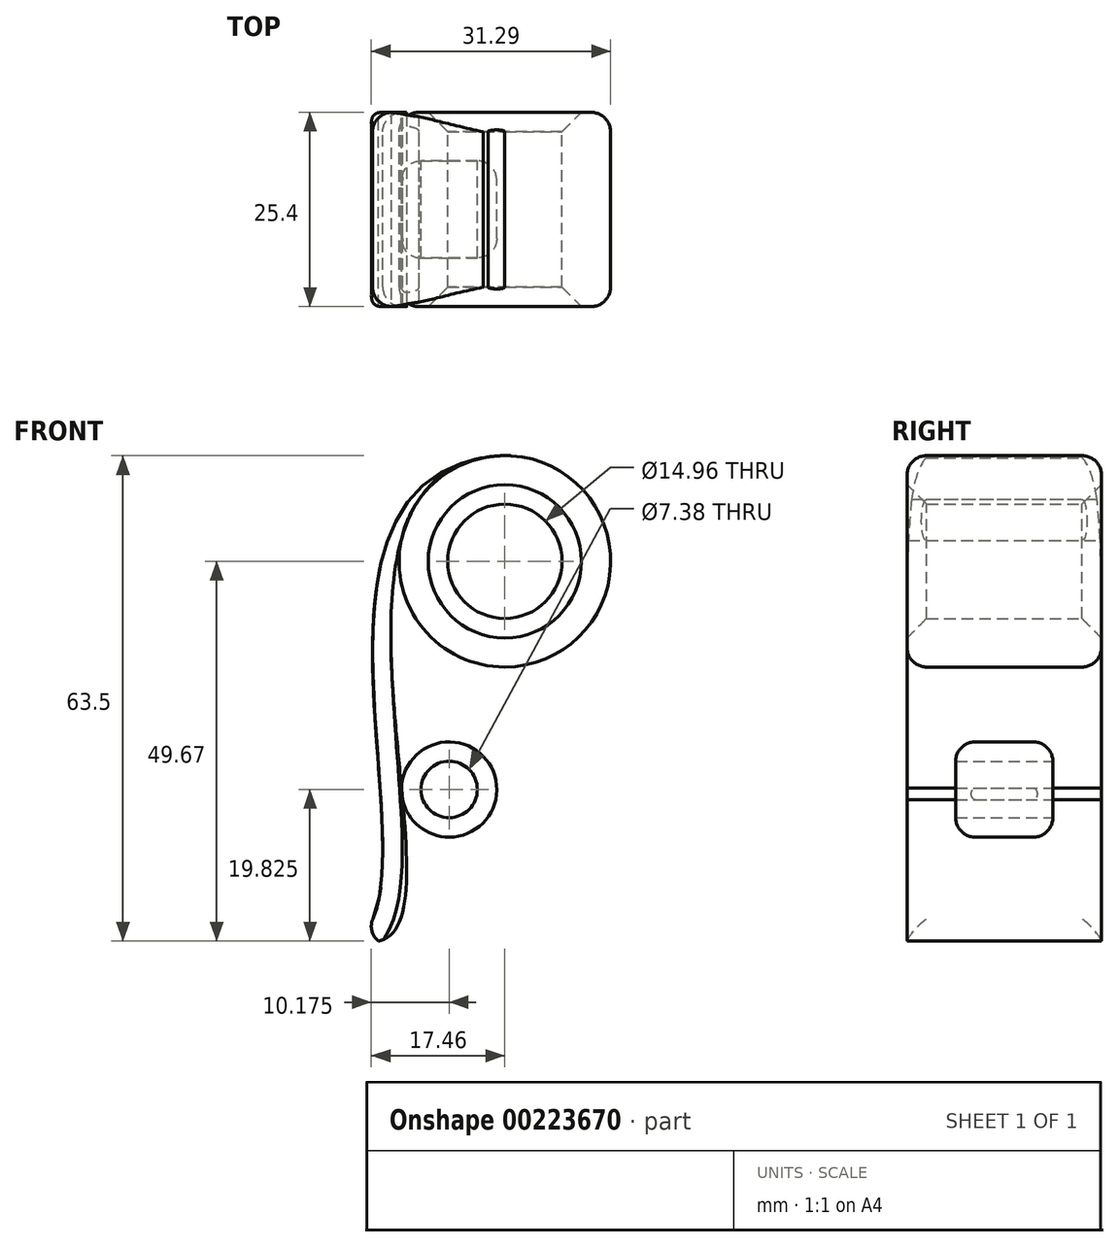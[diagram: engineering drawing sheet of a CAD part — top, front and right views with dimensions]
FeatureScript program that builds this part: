
annotation { "Feature Type Name" : "Feature", "Feature Type Description" : "" }
export const myFeature = defineFeature(function(context is Context, id is Id, definition is map)
    precondition{}
    {
        {
            var Q0;
            Q0=qCreatedBy(makeId("Front.planeOp"),FACE);
            var sketch = newSketch(context, id + "F0", { "sketchPlane" : qUnion([Q0])});
            skCircle(sketch, "E0", {"center": v(0, 0) * mm, "radius": 13.83 * mm});
            skCircle(sketch, "E1", {"center": v(0, 0) * mm, "radius": 7.48 * mm});
            skFitSpline(sketch, "E2", {"points": [v(0, 13.83) * mm, v(-16.56, -49.67) * mm], "startDerivative": vector(-87.8, -2.03) * mm, "endDerivative": vector(-37.2, -6.56) * mm});
            skCircle(sketch, "E3", {"center": v(-7.29, -29.84) * mm, "radius": 6.23 * mm});
            skCircle(sketch, "E4", {"center": v(-7.29, -29.84) * mm, "radius": 3.69 * mm});
            skFitSpline(sketch, "E5", {"points": [v(-2.73, 13.57) * mm, v(-20.14, -49.93) * mm], "startDerivative": vector(-83.92, -14.8) * mm, "endDerivative": vector(-38.31, -17.67) * mm});
            skLineSegment(sketch, "E6", {"start": v(-16.56, -49.67) * mm, "end": v(-20.14, -49.93) * mm});
            skSolve(sketch);
        }
        {
            var Q0;
            {var subQ0=sQuery(id+"F0.wireOp",EDGE,"E6");Q0=makeQuery(id+"F0.imprint","IMPRINT",FACE,{"disambiguationData":[TD([[makeQuery(id+"F0.imprint","IMPRINT",EDGE,{"derivedFrom":subQ0}),-1.0]])]});}
            extrude(context, id + "F1", {"entities" : qUnion([Q0]), "endBound" : BoundingType.SYMMETRIC, "depth" : 25.4 * mm});
        }
        {
            var Q0;
            Q0=makeQuery(id+"F0.imprint","IMPRINT",FACE,{"disambiguationData":[TD([[makeQuery(id+"F0.imprint","IMPRINT",EDGE,{"derivedFrom":sQuery(id+"F0.wireOp",EDGE,"E1")}),-1.0]])]});
            extrude(context, id + "F2", {"entities" : qUnion([Q0]), "endBound" : BoundingType.SYMMETRIC, "depth" : 25.4 * mm});
        }
        {
            var Q0;
            Q0=makeQuery(id+"F0.imprint","IMPRINT",FACE,{"disambiguationData":[TD([[makeQuery(id+"F0.imprint","IMPRINT",EDGE,{"derivedFrom":sQuery(id+"F0.wireOp",EDGE,"E4")}),-1.0]])]});
            extrude(context, id + "F3", {"entities" : qUnion([Q0]), "endBound" : BoundingType.SYMMETRIC, "depth" : 12.7 * mm});
        }
        {
            var Q0;
            Q0=makeQuery(id+"F3.opExtrude","CAP_EDGE",EDGE,{"disambiguationData":[OSD([sQuery(id+"F0.wireOp",EDGE,"E3")])],"isStart":true});
            var Q1;
            Q1=makeQuery(id+"F3.opExtrude","CAP_EDGE",EDGE,{"disambiguationData":[OSD([sQuery(id+"F0.wireOp",EDGE,"E3")])],"isStart":false});
            fillet(context, id + "F4", {"entities" : qUnion([Q0, Q1]), "radius" : 2.54 * mm, "tangentPropagation" : true, "allowEdgeOverflow" : false});
        }
        {
            var Q0;
            {var subQ0=sQuery(id+"F0.wireOp",EDGE,"E2");var subQ1=sQuery(id+"F0.wireOp",EDGE,"E0");Q0=makeQuery(id+"F2.opExtrude","CAP_EDGE",EDGE,{"disambiguationData":[OSD([subQ1]),TDD([makeQuery(id+"F0.imprint","IMPRINT",EDGE,{"disambiguationData":[TD([[makeQuery(id+"F0.imprint","INTERSECT",VERTEX,{"disambiguationData":[OD(0.0)],"derivedFrom":[subQ1,subQ0]}),1.0]])],"derivedFrom":subQ1})])],"isStart":false});}
            var Q1;
            {var subQ0=sQuery(id+"F0.wireOp",EDGE,"E2");var subQ1=sQuery(id+"F0.wireOp",EDGE,"E0");Q1=makeQuery(id+"F2.opExtrude","CAP_EDGE",EDGE,{"disambiguationData":[OSD([subQ1]),TDD([makeQuery(id+"F0.imprint","IMPRINT",EDGE,{"disambiguationData":[TD([[makeQuery(id+"F0.imprint","INTERSECT",VERTEX,{"disambiguationData":[OD(0.0)],"derivedFrom":[subQ1,subQ0]}),1.0]])],"derivedFrom":subQ1})])],"isStart":true});}
            fillet(context, id + "F5", {"entities" : qUnion([Q0, Q1]), "radius" : 2.54 * mm, "tangentPropagation" : true, "allowEdgeOverflow" : false});
        }
        {
            var Q0;
            Q0=makeQuery(id+"F2.opExtrude","CAP_EDGE",EDGE,{"disambiguationData":[OSD([sQuery(id+"F0.wireOp",EDGE,"E1")])],"isStart":true});
            var Q1;
            Q1=makeQuery(id+"F2.opExtrude","CAP_EDGE",EDGE,{"disambiguationData":[OSD([sQuery(id+"F0.wireOp",EDGE,"E1")])],"isStart":false});
            chamfer(context, id + "F6", {"entities" : qUnion([Q0, Q1]), "width" : 2.54 * mm, "tangentPropagation" : true});
        }
        {
            var Q0;
            Q0=makeQuery(id+"F1.opExtrude","SWEPT_EDGE",EDGE,{"disambiguationData":[OSD([sQuery(id+"F0.wireOp",EDGE,"E5"),sQuery(id+"F0.wireOp",EDGE,"E6")])]});
            fillet(context, id + "F7", {"entities" : qUnion([Q0]), "radius" : 2.54 * mm, "tangentPropagation" : true, "allowEdgeOverflow" : false});
        }
        {
            var Q0;
            Q0=makeQuery(id+"F1.opExtrude","CAP_EDGE",EDGE,{"disambiguationData":[OSD([sQuery(id+"F0.wireOp",EDGE,"E5")])],"isStart":false});
            var Q1;
            Q1=makeQuery(id+"F1.opExtrude","CAP_EDGE",EDGE,{"disambiguationData":[OSD([sQuery(id+"F0.wireOp",EDGE,"E5")])],"isStart":true});
            fillet(context, id + "F8", {"entities" : qUnion([Q0, Q1]), "radius" : 2.54 * mm, "tangentPropagation" : true, "allowEdgeOverflow" : false});
        }
    });
